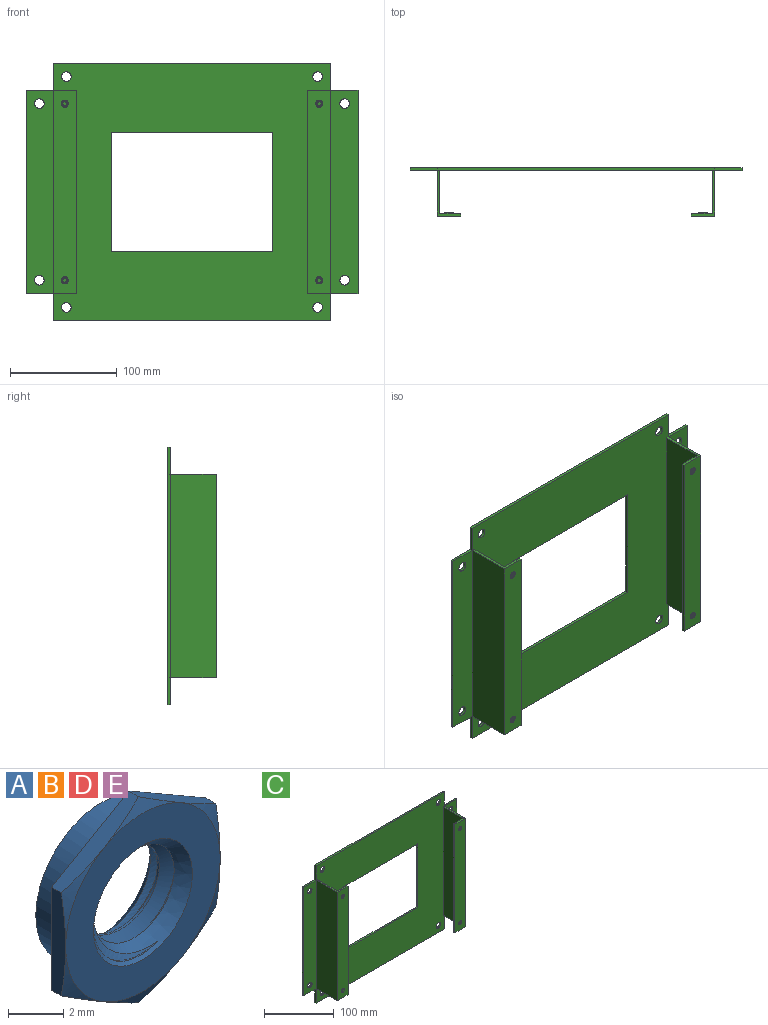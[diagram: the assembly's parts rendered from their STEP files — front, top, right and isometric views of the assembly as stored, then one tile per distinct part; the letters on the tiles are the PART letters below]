
ASSEMBLY  parts=5 mates=4
PART A: 23 faces, bbox 9.5x3x9.5 mm
  f0: plane 4.32x2.64mm, normal (0.5,0,0.87), area 3mm2, adj f1,f5,f12,f21,f22
  f1: plane 4.93x1.09mm, normal (1,0,0), area 3mm2, adj f0,f2,f12,f17,f22
  f2: plane 4.32x2.64mm, normal (0.5,0,-0.87), area 3mm2, adj f1,f3,f12,f17,f18
  f3: plane 4.32x2.64mm, normal (-0.5,0,-0.87), area 3mm2, adj f2,f4,f12,f18,f19
  f4: plane 4.93x1.09mm, normal (-1,0,0), area 3mm2, adj f3,f5,f12,f19,f20
  f5: plane 4.32x2.64mm, normal (-0.5,0,0.87), area 3mm2, adj f0,f4,f12,f20,f21
  f6: plane 7.94x7.94mm, normal (0,-1,0), area 29.2mm2, adj f14,f17,f18,f19,f20,f21,f22
  f7: bspline ~5.58x4.84mm, area 14.3mm2, adj f8,f10,f14,f15
  f8: cylinder r=1.9mm len=3.8mm, axis (0,-1,0), area 1.3mm2, adj f7,f9,f14,f15,f16
  f9: bspline ~5.57x4.83mm, area 14.3mm2, adj f8,f10,f14,f15,f16
  f10: cylinder r=2.41mm len=4.83mm, axis (0,-1,0), area 3.5mm2, adj f7,f9,f14,f15
  f11: cylinder r=3.34mm len=6.68mm, axis (0,1,0), area 29.9mm2, adj f12,f13
  f12: plane 9.17x7.94mm, normal (0,1,0), area 19.5mm2, adj f0,f1,f2,f3,f4,f5,f11
  f13: plane 6.68x6.68mm, normal (0,1,0), area 14.8mm2, adj f11,f15
  f14: cone r=2.54mm half-angle=45deg, axis (0,-1,0), area 7.9mm2, adj f6,f7,f8,f9,f10
  f15: cone r=2.54mm half-angle=45deg, axis (0,1,0), area 7.8mm2, adj f7,f8,f9,f10,f13,f16
  f16: cone r=2.54mm half-angle=45deg, axis (0,1,0), area 0.1mm2, adj f8,f9,f15
  f17: cone r=3.97mm half-angle=70deg, axis (0,1,0), area 1.4mm2, adj f1,f2,f6
  f18: cone r=3.97mm half-angle=70deg, axis (0,1,0), area 1.4mm2, adj f2,f3,f6
  f19: cone r=3.97mm half-angle=70deg, axis (0,1,0), area 1.4mm2, adj f3,f4,f6
  f20: cone r=3.97mm half-angle=70deg, axis (0,1,0), area 1.4mm2, adj f4,f5,f6
  f21: cone r=3.97mm half-angle=70deg, axis (0,1,0), area 1.4mm2, adj f0,f5,f6
  f22: cone r=3.97mm half-angle=70deg, axis (0,1,0), area 1.4mm2, adj f0,f1,f6
PART B: same geometry as A
PART C: 46 faces, bbox 311.6x45.5x241.6 mm
  f0: plane 260.8x241.6mm, normal (0,-1,0), area 44776.8mm2, adj f2,f6,f8,f9,f12,f14,f15,f17
  f1: plane 311.6x241.6mm, normal (0,1,0), area 55169mm2, adj f5,f6,f7,f8,f9,f10,f11,f12
  f2: plane 190.8x40.5mm, normal (1,0,0), area 7727.4mm2, adj f0,f17,f19,f26
  f3: plane 190.8x25.4mm, normal (0,-1,0), area 4719.1mm2, adj f5,f13,f16,f21,f40,f41
  f4: plane 190.8x25.4mm, normal (0,-1,0), area 4719.1mm2, adj f7,f10,f11,f18,f38,f39
  f5: plane 190.8x2.5mm, normal (1,0,0), area 477mm2, adj f1,f3,f13,f16
  f6: plane 260.8x2.5mm, normal (0,0,1), area 652mm2, adj f0,f1,f12,f15
  f7: plane 190.8x2.5mm, normal (-1,0,0), area 477mm2, adj f1,f4,f10,f11
  f8: plane 260.8x2.5mm, normal (0,0,-1), area 652mm2, adj f0,f1,f9,f14
  f9: plane 25.4x2.5mm, normal (-1,0,0), area 63.5mm2, adj f0,f1,f8,f10
  f10: plane 25.4x2.5mm, normal (0,0,-1), area 63.5mm2, adj f1,f4,f7,f9
  f11: plane 25.4x2.5mm, normal (0,0,1), area 63.5mm2, adj f1,f4,f7,f12
  f12: plane 25.4x2.5mm, normal (-1,0,0), area 63.5mm2, adj f0,f1,f6,f11
  f13: plane 25.4x2.5mm, normal (0,0,-1), area 63.5mm2, adj f1,f3,f5,f14
  f14: plane 25.4x2.5mm, normal (1,0,0), area 63.5mm2, adj f0,f1,f8,f13
  f15: plane 25.4x2.5mm, normal (1,0,0), area 63.5mm2, adj f0,f1,f6,f16
  f16: plane 25.4x2.5mm, normal (0,0,1), area 63.5mm2, adj f1,f3,f5,f15
  f17: plane 43x22mm, normal (0,0,1), area 156.2mm2, adj f0,f2,f18,f20,f26,f27
  f18: plane 190.8x43mm, normal (-1,0,0), area 8204.4mm2, adj f4,f17,f19,f20
  f19: plane 43x22mm, normal (0,0,-1), area 156.2mm2, adj f0,f2,f18,f20,f26,f27
  f20: plane 190.8x22mm, normal (0,-1,0), area 4126.4mm2, adj f17,f18,f19,f27,f32,f33
  f21: plane 190.8x43mm, normal (1,0,0), area 8204.4mm2, adj f3,f22,f24,f25
  f22: plane 43x22mm, normal (0,0,1), area 156.2mm2, adj f0,f21,f23,f25,f28,f29
  f23: plane 190.8x40.5mm, normal (-1,0,0), area 7727.4mm2, adj f0,f22,f24,f28
  f24: plane 43x22mm, normal (0,0,-1), area 156.2mm2, adj f0,f21,f23,f25,f28,f29
  f25: plane 190.8x22mm, normal (0,-1,0), area 4126.4mm2, adj f21,f22,f24,f29,f30,f31
  f26: plane 190.8x19.5mm, normal (0,1,0), area 3649.4mm2, adj f2,f17,f19,f27,f32,f33
  f27: plane 190.8x2.5mm, normal (1,0,0), area 477mm2, adj f17,f19,f20,f26
  f28: plane 190.8x19.5mm, normal (0,1,0), area 3649.4mm2, adj f22,f23,f24,f29,f30,f31
  f29: plane 190.8x2.5mm, normal (-1,0,0), area 477mm2, adj f22,f24,f25,f28
  f30: cylinder r=3.37mm len=6.73mm, axis (0,1,0), area 52.9mm2, adj f25,f28
  f31: cylinder r=3.37mm len=6.73mm, axis (0,1,0), area 52.9mm2, adj f25,f28
  f32: cylinder r=3.37mm len=6.73mm, axis (0,1,0), area 52.9mm2, adj f20,f26
  f33: cylinder r=3.37mm len=6.73mm, axis (0,1,0), area 52.9mm2, adj f20,f26
  f34: plane 112x2.5mm, normal (-1,0,0), area 280mm2, adj f0,f1,f35,f37
  f35: plane 152x2.5mm, normal (0,0,-1), area 380mm2, adj f0,f1,f34,f36
  f36: plane 112x2.5mm, normal (1,0,0), area 280mm2, adj f0,f1,f35,f37
  f37: plane 152x2.5mm, normal (0,0,1), area 380mm2, adj f0,f1,f34,f36
  f38: cylinder r=4.5mm len=9mm, axis (0,-1,0), area 70.7mm2, adj f1,f4
  f39: cylinder r=4.5mm len=9mm, axis (0,-1,0), area 70.7mm2, adj f1,f4
  f40: cylinder r=4.5mm len=9mm, axis (0,-1,0), area 70.7mm2, adj f1,f3
  f41: cylinder r=4.5mm len=9mm, axis (0,-1,0), area 70.7mm2, adj f1,f3
  f42: cylinder r=4.5mm len=9mm, axis (0,-1,0), area 70.7mm2, adj f0,f1
  f43: cylinder r=4.5mm len=9mm, axis (0,-1,0), area 70.7mm2, adj f0,f1
  f44: cylinder r=4.5mm len=9mm, axis (0,-1,0), area 70.7mm2, adj f0,f1
  f45: cylinder r=4.5mm len=9mm, axis (0,-1,0), area 70.7mm2, adj f0,f1
PART D: same geometry as A
PART E: same geometry as A
PLACE A rot(axis=(-1,0,0),180deg) t=(-153.47,-54.07,60.19)mm
PLACE B rot(axis=(1,0,0),180deg) t=(85.33,-54.07,-105.61)mm
PLACE C t=(-34.07,-11.81,-22.71)mm
PLACE D rot(axis=(-1,0,0),180deg) t=(-153.47,-54.07,-105.61)mm
PLACE E rot(axis=(1,0,0),180deg) t=(85.33,-54.07,60.19)mm
MATE fastened E.f8 <-> C.f30  axis (0,1,0) through (85.33,-54.07,60.19)mm
MATE fastened A.f8 <-> C.f33  axis (0,1,0) through (-153.47,-54.07,60.19)mm
MATE fastened B.f8 <-> C.f31  axis (0,1,0) through (85.33,-54.07,-105.61)mm
MATE fastened D.f8 <-> C.f32  axis (0,1,0) through (-153.47,-54.07,-105.61)mm
